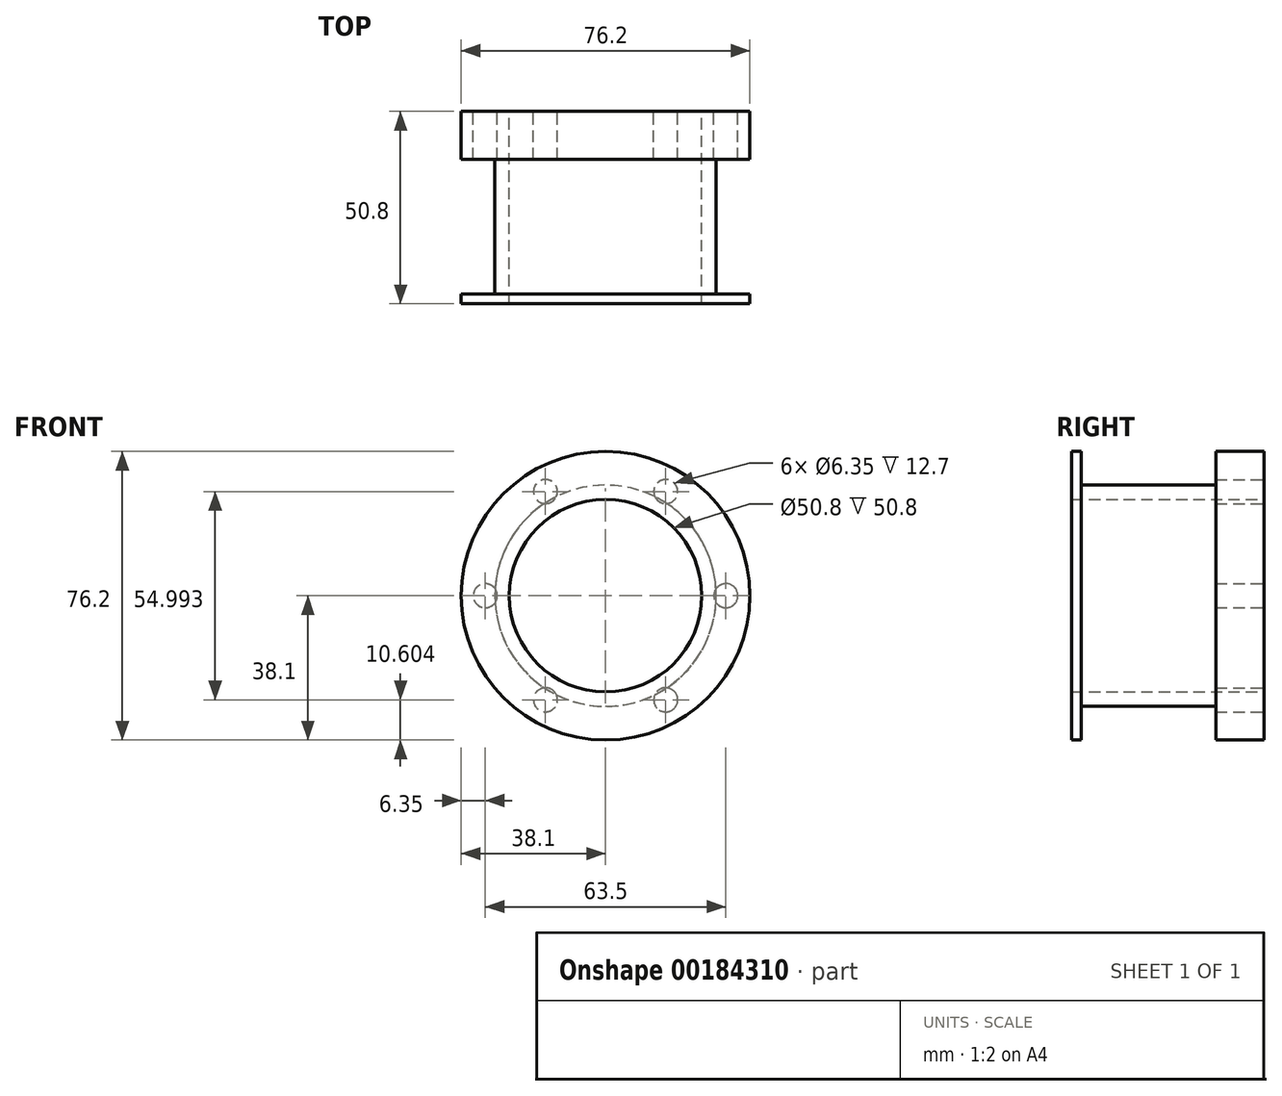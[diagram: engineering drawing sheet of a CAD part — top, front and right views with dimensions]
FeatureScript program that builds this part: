
annotation { "Feature Type Name" : "Feature", "Feature Type Description" : "" }
export const myFeature = defineFeature(function(context is Context, id is Id, definition is map)
    precondition{}
    {
        {
            var Q0;
            Q0=qCreatedBy(makeId("Front.planeOp"),FACE);
            var sketch = newSketch(context, id + "F0", { "sketchPlane" : qUnion([Q0])});
            skCircle(sketch, "E0", {"center": v(0, 0) * mm, "radius": 38.1 * mm});
            skCircle(sketch, "E1", {"center": v(0, 0) * mm, "radius": 25.4 * mm});
            skCircle(sketch, "E2", {"center": v(0, 0) * mm, "radius": 29.21 * mm});
            skSolve(sketch);
        }
        {
            var Q0;
            Q0=makeQuery(id+"F0.imprint","IMPRINT",FACE,{"disambiguationData":[TD([[makeQuery(id+"F0.imprint","IMPRINT",EDGE,{"derivedFrom":sQuery(id+"F0.wireOp",EDGE,"E1")}),-1.0]])]});
            extrude(context, id + "F1", {"entities" : qUnion([Q0]), "depth" : 50.8 * mm});
        }
        {
            var Q0;
            Q0=makeQuery(id+"F0.imprint","IMPRINT",FACE,{"disambiguationData":[TD([[makeQuery(id+"F0.imprint","IMPRINT",EDGE,{"derivedFrom":sQuery(id+"F0.wireOp",EDGE,"E0")}),1.0]])]});
            extrude(context, id + "F2", {"entities" : qUnion([Q0]), "operationType" : NewBodyOperationType.ADD, "depth" : 12.7 * mm});
        }
        {
            var Q0;
            Q0=makeQuery(id+"F0.imprint","IMPRINT",FACE,{"disambiguationData":[TD([[makeQuery(id+"F0.imprint","IMPRINT",EDGE,{"derivedFrom":sQuery(id+"F0.wireOp",EDGE,"E0")}),1.0]])]});
            var sketch = newSketch(context, id + "F3", { "sketchPlane" : qUnion([Q0])});
            skLineSegment(sketch, "E3", {"start": v(0, 0) * mm, "end": v(-31.75, 0) * mm, "construction": true});
            skCircle(sketch, "E4", {"center": v(-31.75, 0) * mm, "radius": 3.18 * mm});
            skCircle(sketch, "E5.1.0", {"center": v(-15.88, -27.5) * mm, "radius": 3.18 * mm});
            skCircle(sketch, "E5.2.0", {"center": v(15.87, -27.5) * mm, "radius": 3.18 * mm});
            skCircle(sketch, "E5.3.0", {"center": v(31.75, 0) * mm, "radius": 3.18 * mm});
            skCircle(sketch, "E5.4.0", {"center": v(15.88, 27.5) * mm, "radius": 3.18 * mm});
            skCircle(sketch, "E5.5.0", {"center": v(-15.88, 27.5) * mm, "radius": 3.18 * mm});
            skPoint(sketch, "E5.center", {"position": v(0, 0) * mm});
            skSolve(sketch);
        }
        {
            var Q0;
            Q0 = qSketchRegion(id + "F3", true);
            extrude(context, id + "F4", {"entities" : qUnion([Q0]), "operationType" : NewBodyOperationType.REMOVE, "depth" : 12.7 * mm});
        }
        {
            var Q0;
            Q0=makeQuery(id+"F1.opExtrude","CAP_FACE",FACE,{"disambiguationData":[OSD([sQuery(id+"F0.wireOp",EDGE,"E1"),sQuery(id+"F0.wireOp",EDGE,"E2")])],"isStart":false});
            var sketch = newSketch(context, id + "F5", { "sketchPlane" : qUnion([Q0])});
            skCircle(sketch, "E6", {"center": v(0, 0) * mm, "radius": 38.1 * mm});
            skCircle(sketch, "E7", {"center": v(0, 0) * mm, "radius": 25.4 * mm});
            skSolve(sketch);
        }
        {
            var Q0;
            Q0 = qSketchRegion(id + "F5", true);
            extrude(context, id + "F6", {"entities" : qUnion([Q0]), "operationType" : NewBodyOperationType.ADD, "oppositeDirection" : true, "depth" : 2.54 * mm});
        }
    });
